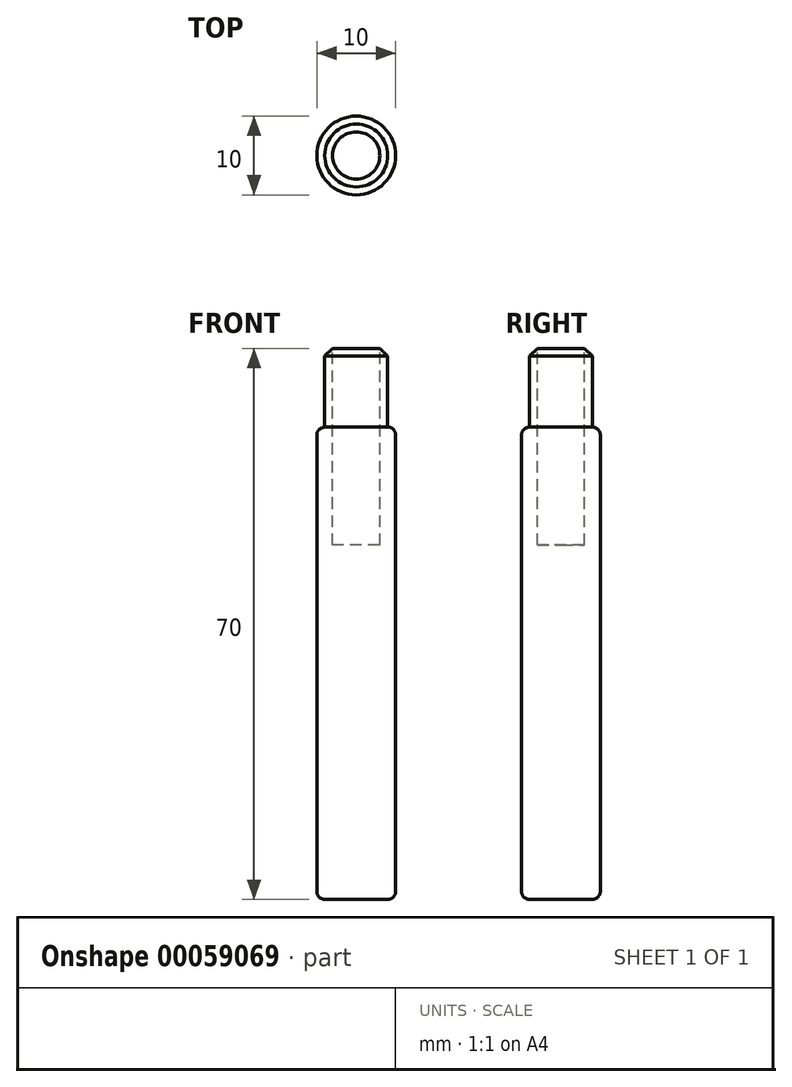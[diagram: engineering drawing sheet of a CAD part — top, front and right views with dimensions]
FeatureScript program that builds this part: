
annotation { "Feature Type Name" : "Feature", "Feature Type Description" : "" }
export const myFeature = defineFeature(function(context is Context, id is Id, definition is map)
    precondition{}
    {
        {
            var Q0;
            Q0=qCreatedBy(makeId("Top.planeOp"),FACE);
            var sketch = newSketch(context, id + "F0", { "sketchPlane" : qUnion([Q0])});
            skCircle(sketch, "E0", {"center": v(0, 0) * mm, "radius": 5 * mm});
            skSolve(sketch);
        }
        {
            var Q0;
            Q0 = qSketchRegion(id + "F0", true);
            extrude(context, id + "F1", {"entities" : qUnion([Q0]), "depth" : 50 * mm});
        }
        {
            var Q0;
            Q0=makeQuery(id+"F1.opExtrude","CAP_EDGE",EDGE,{"disambiguationData":[OSD([sQuery(id+"F0.wireOp",EDGE,"E0")])],"isStart":true});
            fillet(context, id + "F2", {"entities" : qUnion([Q0]), "radius" : 1 * mm, "tangentPropagation" : true, "allowEdgeOverflow" : false});
        }
        {
            var Q0;
            Q0=makeQuery(id+"F1.opExtrude","CAP_FACE",FACE,{"disambiguationData":[OSD([sQuery(id+"F0.wireOp",EDGE,"E0")])],"isStart":false});
            extrude(context, id + "F3", {"entities" : qUnion([Q0]), "operationType" : NewBodyOperationType.ADD, "depth" : 10 * mm});
        }
        {
            var Q0;
            Q0=makeQuery(id+"F3.opExtrude","CAP_EDGE",EDGE,{"disambiguationData":[OSD([sQuery(id+"F0.wireOp",EDGE,"E0")])],"isStart":false});
            fillet(context, id + "F4", {"entities" : qUnion([Q0]), "radius" : 1 * mm, "tangentPropagation" : true, "allowEdgeOverflow" : false});
        }
        {
            var Q0;
            Q0=makeQuery(id+"F3.opExtrude","CAP_FACE",FACE,{"disambiguationData":[OSD([sQuery(id+"F0.wireOp",EDGE,"E0")])],"isStart":false});
            var sketch = newSketch(context, id + "F5", { "sketchPlane" : qUnion([Q0])});
            skSolve(sketch);
        }
        {
            var Q0;
            {var subQ0=sQuery(id+"F0.wireOp",EDGE,"E0");Q0=makeQuery(id+"F5.imprint","IMPRINT",FACE,{"disambiguationData":[TD([[makeQuery(id+"F5.imprint","IMPRINT",EDGE,{"derivedFrom":makeQuery(id+"F4.opFillet","BLEND_EDGE",EDGE,{"blendedFrom":[makeQuery(id+"F3.opExtrude","CAP_EDGE",EDGE,{"disambiguationData":[OSD([subQ0])],"isStart":false}),makeQuery(id+"F3.opExtrude","CAP_FACE",FACE,{"disambiguationData":[OSD([subQ0])],"isStart":false})],"blendedInto":[makeQuery(id+"F3.opExtrude","CAP_FACE",FACE,{"disambiguationData":[OSD([subQ0])],"isStart":false})]})}),1.0]])]});}
            extrude(context, id + "F6", {"entities" : qUnion([Q0]), "depth" : 10 * mm});
        }
        {
            var Q0;
            Q0=makeQuery(id+"F6.opExtrude","CAP_EDGE",EDGE,{"disambiguationData":[OSD([sQuery(id+"F0.wireOp",EDGE,"E0")])],"isStart":false});
            chamfer(context, id + "F7", {"entities" : qUnion([Q0]), "width" : 1 * mm, "tangentPropagation" : true});
        }
        {
            var Q0;
            Q0=makeQuery(id+"F6.opExtrude","CAP_FACE",FACE,{"disambiguationData":[OSD([sQuery(id+"F0.wireOp",EDGE,"E0")])],"isStart":false});
            extrude(context, id + "F8", {"entities" : qUnion([Q0]), "oppositeDirection" : true, "depth" : 25 * mm});
        }
    });
